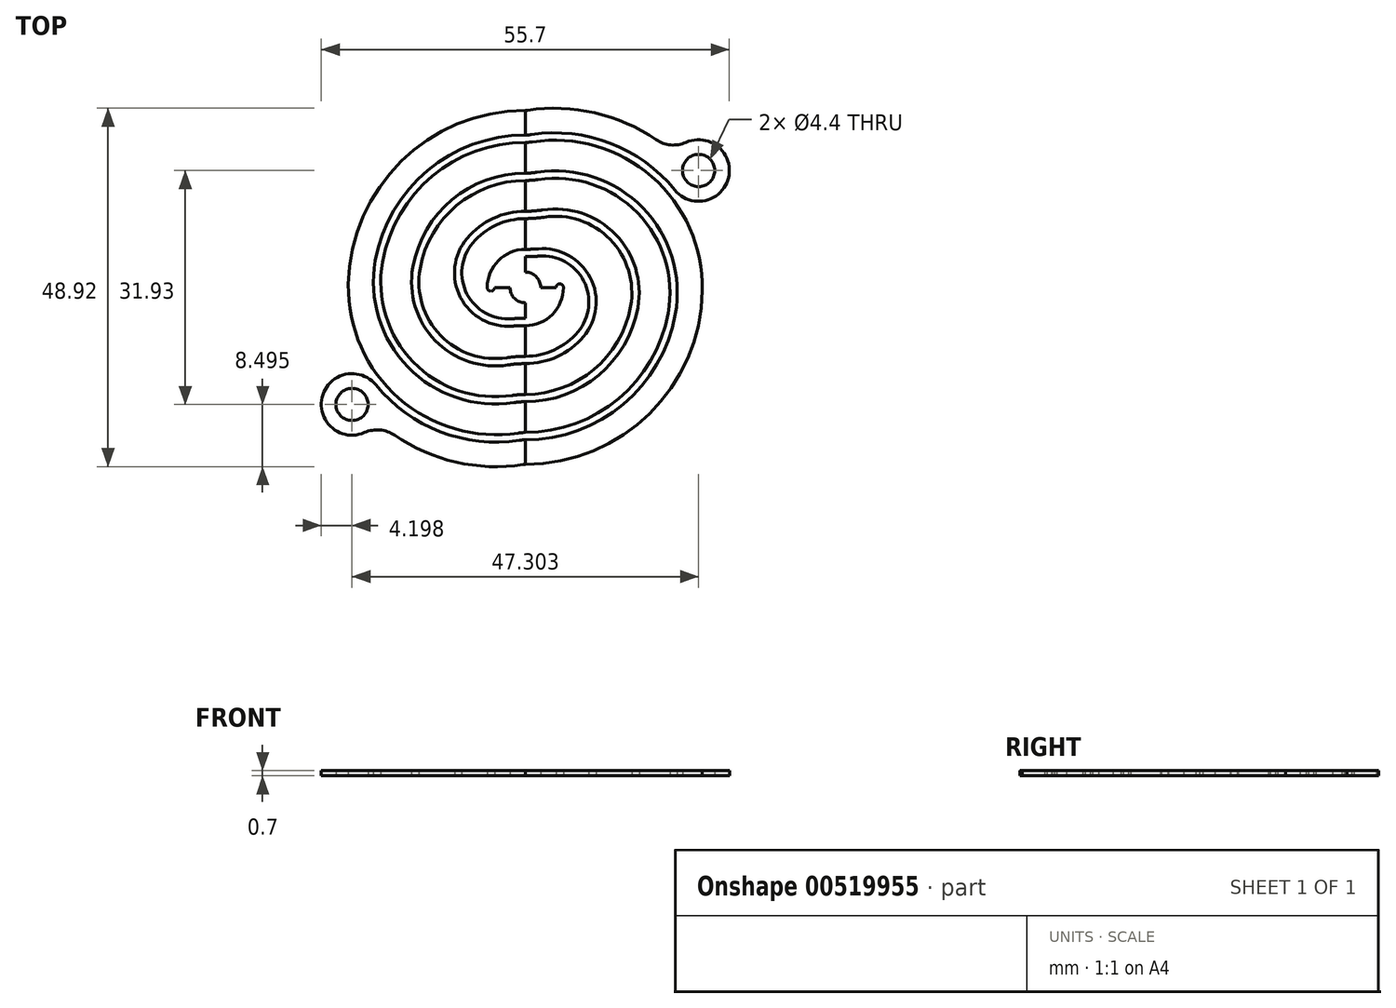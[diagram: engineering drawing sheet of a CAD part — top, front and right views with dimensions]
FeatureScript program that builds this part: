
annotation { "Feature Type Name" : "Feature", "Feature Type Description" : "" }
export const myFeature = defineFeature(function(context is Context, id is Id, definition is map)
    precondition{}
    {
        {
            var Q0;
            Q0=qCreatedBy(makeId("Top.planeOp"),FACE);
            var sketch = newSketch(context, id + "F0", { "sketchPlane" : qUnion([Q0])});
            skCircle(sketch, "E0", {"center": v(0, 0) * mm, "radius": 2.1 * mm, "construction": true});
            skArc(sketch, "E1.0", {"start": v(13.08, 8.5) * mm, "mid": v(13.07, 8.51) * mm, "end": v(13.06, 8.53) * mm, "construction": true});
            skArc(sketch, "E2.0", {"start": v(8.24, 18) * mm, "mid": v(7.74, 18.23) * mm, "end": v(7.23, 18.43) * mm, "construction": true});
            skArc(sketch, "E3.0", {"start": v(0, 20.8) * mm, "mid": v(-14.7, -14.7) * mm, "end": v(20.8, 0) * mm, "construction": true});
            skArc(sketch, "E4.0", {"start": v(-4.81, 23.68) * mm, "mid": v(-12.28, -20.8) * mm, "end": v(23.05, 7.24) * mm, "construction": true});
            skCircle(sketch, "E5.converted", {"center": v(0, 0) * mm, "radius": 4.2 * mm, "construction": true});
            skCircle(sketch, "E6.converted", {"center": v(0, 0) * mm, "radius": 5.2 * mm, "construction": true});
            skArc(sketch, "E7.converted", {"start": v(0, 9.4) * mm, "mid": v(-8.53, -3.96) * mm, "end": v(7.18, -6.07) * mm, "construction": true});
            skArc(sketch, "E8.converted", {"start": v(3.6, 9.75) * mm, "mid": v(3.58, 9.77) * mm, "end": v(3.55, 9.78) * mm, "construction": true});
            skArc(sketch, "E9", {"start": v(0, 14.6) * mm, "mid": v(-4.54, 13.88) * mm, "end": v(-8.63, 11.78) * mm, "construction": true});
            skArc(sketch, "E10", {"start": v(18.7, 16.59) * mm, "mid": v(-23.37, -8.87) * mm, "end": v(25, 0) * mm, "construction": true});
            skCircle(sketch, "E11", {"center": v(0, 26.26) * mm, "radius": 24.16 * mm, "construction": true});
            skCircle(sketch, "E12", {"center": v(0, 26.26) * mm, "radius": 22.06 * mm, "construction": true});
            skCircle(sketch, "E13", {"center": v(0, 26.26) * mm, "radius": 21.06 * mm, "construction": true});
            skArc(sketch, "E14", {"start": v(-3.55, 9.78) * mm, "mid": v(2.73, 9.62) * mm, "end": v(8.63, 11.78) * mm, "construction": true});
            skCircle(sketch, "E15", {"center": v(0, 26.26) * mm, "radius": 11.66 * mm, "construction": true});
            skCircle(sketch, "E16", {"center": v(0, 26.26) * mm, "radius": 10.66 * mm, "construction": true});
            skArc(sketch, "E17", {"start": v(-5.82, 23.45) * mm, "mid": v(-4.67, 21.8) * mm, "end": v(-3.06, 20.57) * mm, "construction": true});
            skLineSegment(sketch, "E18", {"start": v(2.1, 0) * mm, "end": v(4.2, 0) * mm});
            skLineSegment(sketch, "E19", {"start": v(15.6, 0) * mm, "end": v(19.8, 0) * mm});
            skLineSegment(sketch, "E20", {"start": v(-10.4, 0) * mm, "end": v(-14.6, 0) * mm});
            skLineSegment(sketch, "E21", {"start": v(-15.6, 0) * mm, "end": v(-19.8, 0) * mm});
            skLineSegment(sketch, "E22", {"start": v(-20.8, 0) * mm, "end": v(-24.16, 0) * mm});
            skLineSegment(sketch, "E23", {"start": v(4.2, 0) * mm, "end": v(5.2, 0) * mm, "construction": true});
            skArc(sketch, "E24", {"start": v(5.2, 0) * mm, "mid": v(4.7, 0.5) * mm, "end": v(4.2, 0) * mm});
            skArc(sketch, "E25", {"start": v(0, 4.2) * mm, "mid": v(0.92, 4.22) * mm, "end": v(1.84, 4.28) * mm});
            skArc(sketch, "E26", {"start": v(7.18, -6.07) * mm, "mid": v(-8.53, -3.96) * mm, "end": v(0, 9.4) * mm, "construction": true});
            skPoint(sketch, "E27.visualSharp", {"position": v(7.59, 5.55) * mm});
            skArc(sketch, "E27.filletArc", {"start": v(7.18, -6.07) * mm, "mid": v(7.97, 0.89) * mm, "end": v(1.84, 4.28) * mm});
            skArc(sketch, "E28", {"start": v(0, 4.2) * mm, "mid": v(-2.97, 2.97) * mm, "end": v(-4.2, 0) * mm});
            skArc(sketch, "E29", {"start": v(2.1, 0) * mm, "mid": v(0, 2.1) * mm, "end": v(-2.1, 0) * mm});
            skArc(sketch, "E30", {"start": v(0, 5.2) * mm, "mid": v(-3.68, 3.68) * mm, "end": v(-5.2, 0) * mm});
            skArc(sketch, "E31", {"start": v(0, 5.2) * mm, "mid": v(0.88, 5.22) * mm, "end": v(1.76, 5.27) * mm});
            skArc(sketch, "E32", {"start": v(10.26, 1.72) * mm, "mid": v(9.98, 2.92) * mm, "end": v(9.57, 4.08) * mm, "construction": true});
            skPoint(sketch, "E33.visualSharp", {"position": v(7.92, 6.74) * mm});
            skArc(sketch, "E33.filletArc", {"start": v(7.94, -6.71) * mm, "mid": v(8.85, 1.35) * mm, "end": v(1.76, 5.27) * mm});
            skArc(sketch, "E34", {"start": v(0, 9.4) * mm, "mid": v(1.27, 9.45) * mm, "end": v(2.53, 9.6) * mm});
            skArc(sketch, "E35", {"start": v(13.28, 6.07) * mm, "mid": v(13.27, 6.1) * mm, "end": v(13.26, 6.12) * mm, "construction": true});
            skPoint(sketch, "E36.visualSharp", {"position": v(-8.63, 11.78) * mm});
            skArc(sketch, "E37", {"start": v(0, 9.4) * mm, "mid": v(-6.65, 6.65) * mm, "end": v(-9.4, 0) * mm});
            skArc(sketch, "E38.trimOffspring", {"start": v(0, 10.4) * mm, "mid": v(-9.43, -4.38) * mm, "end": v(7.94, -6.71) * mm, "construction": true});
            skArc(sketch, "E39.trimOffspring", {"start": v(0, 10.4) * mm, "mid": v(-9.43, -4.38) * mm, "end": v(7.94, -6.71) * mm});
            skArc(sketch, "E40", {"start": v(-8.63, 11.78) * mm, "mid": v(-6.6, -13.02) * mm, "end": v(14.6, 0) * mm, "construction": true});
            skArc(sketch, "E41", {"start": v(-8.63, 11.78) * mm, "mid": v(-8.18, 12.1) * mm, "end": v(-7.71, 12.4) * mm});
            skArc(sketch, "E42", {"start": v(-8.63, 11.78) * mm, "mid": v(-13.02, 6.6) * mm, "end": v(-14.6, 0) * mm});
            skLineSegment(sketch, "E43", {"start": v(0, 14.6) * mm, "end": v(0, 14.6) * mm});
            skArc(sketch, "E44", {"start": v(17.74, 8.78) * mm, "mid": v(17.57, 9.13) * mm, "end": v(17.38, 9.48) * mm, "construction": true});
            skPoint(sketch, "E45.visualSharp", {"position": v(8.24, 18) * mm});
            skArc(sketch, "E46.trimOffspring", {"start": v(13.08, 8.5) * mm, "mid": v(13.07, 8.51) * mm, "end": v(13.06, 8.53) * mm});
            skArc(sketch, "E47.trimOffspring", {"start": v(0, 15.6) * mm, "mid": v(-11.03, -11.03) * mm, "end": v(15.6, 0) * mm, "construction": true});
            skArc(sketch, "E48", {"start": v(10.26, 1.72) * mm, "mid": v(9.98, 2.92) * mm, "end": v(9.57, 4.08) * mm});
            skArc(sketch, "E49", {"start": v(-9.71, 12.48) * mm, "mid": v(-3.87, 9.85) * mm, "end": v(2.53, 9.6) * mm, "construction": true});
            skArc(sketch, "E50", {"start": v(13.28, 6.07) * mm, "mid": v(13.27, 6.1) * mm, "end": v(13.26, 6.12) * mm});
            skPoint(sketch, "E51.visualSharp", {"position": v(8.63, 11.78) * mm});
            skArc(sketch, "E51.filletArc", {"start": v(14.37, -2.57) * mm, "mid": v(11.57, 6.55) * mm, "end": v(2.53, 9.6) * mm});
            skArc(sketch, "E52.trimOffspring", {"start": v(8.63, 11.78) * mm, "mid": v(10.21, 12.85) * mm, "end": v(11.66, 14.09) * mm, "construction": true});
            skArc(sketch, "E53", {"start": v(0, 14.6) * mm, "mid": v(-4.01, 14.04) * mm, "end": v(-7.71, 12.4) * mm});
            skArc(sketch, "E54", {"start": v(0, 15.6) * mm, "mid": v(-11.03, 11.03) * mm, "end": v(-15.6, 0) * mm});
            skArc(sketch, "E55", {"start": v(0, 14.6) * mm, "mid": v(0.88, 14.63) * mm, "end": v(1.75, 14.73) * mm});
            skCircle(sketch, "E56", {"center": v(0, 26.26) * mm, "radius": 15.86 * mm, "construction": true});
            skArc(sketch, "E57", {"start": v(0, 10.4) * mm, "mid": v(1.2, 10.44) * mm, "end": v(2.38, 10.58) * mm});
            skPoint(sketch, "E58.visualSharp", {"position": v(8.66, 12.97) * mm});
            skArc(sketch, "E58.filletArc", {"start": v(15.36, -2.75) * mm, "mid": v(12.3, 7.25) * mm, "end": v(2.38, 10.58) * mm});
            skArc(sketch, "E59", {"start": v(17.74, 8.78) * mm, "mid": v(17.57, 9.13) * mm, "end": v(17.38, 9.48) * mm});
            skArc(sketch, "E60.filletArc", {"start": v(19.5, -3.49) * mm, "mid": v(15.3, 10.18) * mm, "end": v(1.75, 14.73) * mm});
            skArc(sketch, "E61", {"start": v(0, 15.6) * mm, "mid": v(0.8, 15.63) * mm, "end": v(1.6, 15.72) * mm});
            skArc(sketch, "E62", {"start": v(17.42, 11.37) * mm, "mid": v(17.17, 11.74) * mm, "end": v(16.92, 12.1) * mm});
            skPoint(sketch, "E63.visualSharp", {"position": v(8, 19.2) * mm});
            skArc(sketch, "E63.filletArc", {"start": v(20.47, -3.67) * mm, "mid": v(16.02, 10.88) * mm, "end": v(1.6, 15.72) * mm});
            skArc(sketch, "E64", {"start": v(0, 19.8) * mm, "mid": v(-14, 14) * mm, "end": v(-19.8, 0) * mm});
            skArc(sketch, "E65", {"start": v(0, 19.8) * mm, "mid": v(1.58, 32.52) * mm, "end": v(-3.06, 20.57) * mm, "construction": true});
            skArc(sketch, "E66.trimOffspring", {"start": v(12.7, 15.18) * mm, "mid": v(12.32, 15.5) * mm, "end": v(11.93, 15.8) * mm, "construction": true});
            skArc(sketch, "E67.trimOffspring", {"start": v(16.58, 10.82) * mm, "mid": v(16.41, 11.08) * mm, "end": v(16.24, 11.33) * mm, "construction": true});
            skArc(sketch, "E68", {"start": v(24.16, 0) * mm, "mid": v(23.88, 3.66) * mm, "end": v(23.05, 7.24) * mm});
            skPoint(sketch, "E69.visualSharp", {"position": v(5.82, 23.45) * mm});
            skArc(sketch, "E70.trimOffspring", {"start": v(11.66, 14.09) * mm, "mid": v(-1.26, 43.07) * mm, "end": v(-9.71, 12.48) * mm, "construction": true});
            skArc(sketch, "E71.trimOffspring", {"start": v(10.86, 13.37) * mm, "mid": v(11.27, 13.72) * mm, "end": v(11.66, 14.09) * mm, "construction": true});
            skArc(sketch, "E72", {"start": v(0, 20.8) * mm, "mid": v(-14.7, 14.7) * mm, "end": v(-20.8, 0) * mm});
            skArc(sketch, "E73", {"start": v(0, 24.16) * mm, "mid": v(-17.08, 17.08) * mm, "end": v(-24.16, 0) * mm});
            skArc(sketch, "E74", {"start": v(0, 20.8) * mm, "mid": v(0.41, 20.82) * mm, "end": v(0.82, 20.86) * mm});
            skArc(sketch, "E75", {"start": v(4.81, 23.68) * mm, "mid": v(5, 24.06) * mm, "end": v(5.16, 24.46) * mm});
            skCircle(sketch, "E76.converted", {"center": v(0, 26.26) * mm, "radius": 5.46 * mm, "construction": true});
            skArc(sketch, "E77", {"start": v(0, 19.8) * mm, "mid": v(0.49, 19.82) * mm, "end": v(0.97, 19.87) * mm});
            skArc(sketch, "E78.filletArc", {"start": v(24.16, -0.4) * mm, "mid": v(17.27, 15.12) * mm, "end": v(0.97, 19.87) * mm});
            skArc(sketch, "E79.0", {"start": v(20.4, 13.31) * mm, "mid": v(11.6, 19.68) * mm, "end": v(0.82, 20.86) * mm});
            skCircle(sketch, "E80.converted", {"center": v(0, 26.26) * mm, "radius": 2.1 * mm, "construction": true});
            skArc(sketch, "E81.0", {"start": v(22.1, 16.48) * mm, "mid": v(21.88, 16.72) * mm, "end": v(21.66, 16.95) * mm, "construction": true});
            skArc(sketch, "E82", {"start": v(0, 24.16) * mm, "mid": v(0.16, 24.17) * mm, "end": v(0.31, 24.18) * mm});
            skLineSegment(sketch, "E83", {"start": v(0, 0) * mm, "end": v(12.23, 7.98) * mm, "construction": true});
            skArc(sketch, "E84.trimOffspring", {"start": v(17.85, 20.17) * mm, "mid": v(9.46, 23.84) * mm, "end": v(0.31, 24.18) * mm});
            skArc(sketch, "E85", {"start": v(20.4, 13.31) * mm, "mid": v(27.74, 15) * mm, "end": v(21.94, 19.8) * mm});
            skCircle(sketch, "E86", {"center": v(23.65, 15.97) * mm, "radius": 2.2 * mm});
            skPoint(sketch, "E87.visualSharp", {"position": v(20.2, 18.35) * mm});
            skArc(sketch, "E87.filletArc", {"start": v(17.85, 20.17) * mm, "mid": v(19.85, 19.45) * mm, "end": v(21.94, 19.8) * mm});
            skLineSegment(sketch, "E88", {"start": v(0, -5.2) * mm, "end": v(0, -9.4) * mm});
            skLineSegment(sketch, "E89", {"start": v(0, -10.4) * mm, "end": v(0, -14.6) * mm});
            skLineSegment(sketch, "E90", {"start": v(0, -15.6) * mm, "end": v(0, -19.8) * mm});
            skLineSegment(sketch, "E91", {"start": v(0, -20.8) * mm, "end": v(0, -24.16) * mm});
            skArc(sketch, "E92", {"start": v(0, -5.2) * mm, "mid": v(3.68, -3.68) * mm, "end": v(5.2, 0) * mm});
            skArc(sketch, "E93", {"start": v(-1.53, -9.28) * mm, "mid": v(3.25, -8.82) * mm, "end": v(7.18, -6.07) * mm});
            skLineSegment(sketch, "E94", {"start": v(0, 2.1) * mm, "end": v(0, 4.2) * mm});
            skLineSegment(sketch, "E95", {"start": v(0, 10.4) * mm, "end": v(0, 14.6) * mm});
            skLineSegment(sketch, "E96", {"start": v(0, 15.6) * mm, "end": v(0, 19.8) * mm});
            skLineSegment(sketch, "E97", {"start": v(0, 20.8) * mm, "end": v(0, 24.16) * mm});
            skLineSegment(sketch, "E98", {"start": v(0, 5.2) * mm, "end": v(0, 9.4) * mm});
            skArc(sketch, "E99", {"start": v(0, -14.6) * mm, "mid": v(10.32, -10.32) * mm, "end": v(14.6, 0) * mm});
            skArc(sketch, "E100.trimOffspring", {"start": v(0, 9.4) * mm, "mid": v(-8.53, -3.96) * mm, "end": v(7.18, -6.07) * mm});
            skArc(sketch, "E101.trimOffspring", {"start": v(3.6, 9.75) * mm, "mid": v(3.58, 9.77) * mm, "end": v(3.55, 9.78) * mm});
            skArc(sketch, "E102.trimOffspring", {"start": v(8.7, 5.68) * mm, "mid": v(8.63, 5.8) * mm, "end": v(8.55, 5.92) * mm});
            skArc(sketch, "E103.trimOffspring", {"start": v(7.87, 5.14) * mm, "mid": v(7.73, 5.34) * mm, "end": v(7.59, 5.55) * mm});
            skArc(sketch, "E104.trimOffspring", {"start": v(9.4, -0.04) * mm, "mid": v(9.36, 0.85) * mm, "end": v(9.24, 1.72) * mm, "construction": true});
            skArc(sketch, "E105.trimOffspring", {"start": v(9.4, -0.04) * mm, "mid": v(9.36, 0.85) * mm, "end": v(9.24, 1.72) * mm});
            skArc(sketch, "E106.trimOffspring", {"start": v(12.26, 7.92) * mm, "mid": v(12.25, 7.95) * mm, "end": v(12.23, 7.98) * mm, "construction": true});
            skArc(sketch, "E107.trimOffspring", {"start": v(12.26, 7.92) * mm, "mid": v(12.25, 7.95) * mm, "end": v(12.23, 7.98) * mm});
            skLineSegment(sketch, "E108.trimOffspring", {"start": v(13.06, 8.53) * mm, "end": v(23.22, 15.16) * mm, "construction": true});
            skArc(sketch, "E109.trimOffspring", {"start": v(0, 14.6) * mm, "mid": v(-11.2, -9.37) * mm, "end": v(14.37, -2.57) * mm});
            skArc(sketch, "E110.trimOffspring", {"start": v(0, 15.6) * mm, "mid": v(-11.96, -10.01) * mm, "end": v(15.36, -2.75) * mm});
            skArc(sketch, "E111.trimOffspring", {"start": v(0, 19.8) * mm, "mid": v(4.57, 21.7) * mm, "end": v(6.46, 26.26) * mm, "construction": true});
            skArc(sketch, "E112.trimOffspring", {"start": v(0, 20.8) * mm, "mid": v(-15.95, -13.35) * mm, "end": v(20.47, -3.67) * mm});
            skArc(sketch, "E113.trimOffspring", {"start": v(0, 19.8) * mm, "mid": v(-16.25, -11.32) * mm, "end": v(18.57, -6.86) * mm, "construction": true});
            skArc(sketch, "E114.trimOffspring", {"start": v(0, 19.8) * mm, "mid": v(-14, -14) * mm, "end": v(19.8, 0) * mm, "construction": true});
            skArc(sketch, "E115.trimOffspring", {"start": v(0, 19.8) * mm, "mid": v(-15.18, -12.7) * mm, "end": v(19.5, -3.49) * mm, "construction": true});
            skArc(sketch, "E116.trimOffspring", {"start": v(0, 19.8) * mm, "mid": v(-15.18, -12.7) * mm, "end": v(19.5, -3.49) * mm});
            skArc(sketch, "E117.trimOffspring", {"start": v(5.58, 20.04) * mm, "mid": v(4.33, 20.34) * mm, "end": v(3.06, 20.57) * mm, "construction": true});
            skArc(sketch, "E118.trimOffspring", {"start": v(5.58, 20.04) * mm, "mid": v(4.33, 20.34) * mm, "end": v(3.06, 20.57) * mm});
            skArc(sketch, "E119", {"start": v(0, -24.16) * mm, "mid": v(19.48, -14.3) * mm, "end": v(23.05, 7.24) * mm});
            skArc(sketch, "E120.trimOffspring", {"start": v(8.24, 18) * mm, "mid": v(7.74, 18.23) * mm, "end": v(7.23, 18.43) * mm});
            skArc(sketch, "E121.trimOffspring", {"start": v(8.94, 18.78) * mm, "mid": v(8.47, 19) * mm, "end": v(8, 19.2) * mm, "construction": true});
            skArc(sketch, "E122.trimOffspring", {"start": v(13.34, 15.96) * mm, "mid": v(12.96, 16.27) * mm, "end": v(12.56, 16.58) * mm, "construction": true});
            skArc(sketch, "E123.trimOffspring", {"start": v(13.34, 15.96) * mm, "mid": v(12.96, 16.27) * mm, "end": v(12.56, 16.58) * mm});
            skArc(sketch, "E124.trimOffspring", {"start": v(17.42, 11.37) * mm, "mid": v(17.17, 11.74) * mm, "end": v(16.92, 12.1) * mm, "construction": true});
            skArc(sketch, "E125.trimOffspring", {"start": v(12.7, 15.18) * mm, "mid": v(12.32, 15.5) * mm, "end": v(11.93, 15.8) * mm});
            skArc(sketch, "E126.trimOffspring", {"start": v(16.58, 10.82) * mm, "mid": v(16.41, 11.08) * mm, "end": v(16.24, 11.33) * mm});
            skArc(sketch, "E127.trimOffspring", {"start": v(20.28, 13.13) * mm, "mid": v(19.33, 14.5) * mm, "end": v(18.28, 15.8) * mm, "construction": true});
            skArc(sketch, "E128.trimOffspring", {"start": v(20.28, 13.13) * mm, "mid": v(19.33, 14.5) * mm, "end": v(18.28, 15.8) * mm});
            skArc(sketch, "E129.trimOffspring", {"start": v(10.71, 21.66) * mm, "mid": v(10.26, 21.87) * mm, "end": v(9.8, 22.08) * mm, "construction": true});
            skArc(sketch, "E130.trimOffspring", {"start": v(10.71, 21.66) * mm, "mid": v(10.26, 21.87) * mm, "end": v(9.8, 22.08) * mm});
            skArc(sketch, "E131.trimOffspring", {"start": v(5.82, 23.45) * mm, "mid": v(5.31, 23.57) * mm, "end": v(4.81, 23.68) * mm});
            skArc(sketch, "E132.trimOffspring", {"start": v(15.14, 18.83) * mm, "mid": v(14.73, 19.15) * mm, "end": v(14.33, 19.45) * mm, "construction": true});
            skArc(sketch, "E133.trimOffspring", {"start": v(15.14, 18.83) * mm, "mid": v(14.73, 19.15) * mm, "end": v(14.33, 19.45) * mm});
            skArc(sketch, "E134.trimOffspring", {"start": v(0, 24.16) * mm, "mid": v(-17.22, -16.94) * mm, "end": v(24.16, -0.4) * mm});
            skSolve(sketch);
        }
        {
            var Q0;
            Q0=makeQuery(id+"F0.imprint","IMPRINT",FACE,{"disambiguationData":[TD([[makeQuery(id+"F0.imprint","IMPRINT",EDGE,{"derivedFrom":sQuery(id+"F0.wireOp",EDGE,"C1ZH9qWL-1q6U-ss44-XQ4E-Uqg7t3fqfPqc")}),-1.0]])]});
            var Q1;
            Q1=makeQuery(id+"F0.imprint","IMPRINT",FACE,{"disambiguationData":[TD([[makeQuery(id+"F0.imprint","IMPRINT",EDGE,{"derivedFrom":sQuery(id+"F0.wireOp",EDGE,"E18")}),1.0]])]});
            var Q2;
            {var subQ1=sQuery(id+"F0.wireOp",EDGE,"E19");Q2=makeQuery(id+"F0.imprint","IMPRINT",FACE,{"disambiguationData":[TD([[makeQuery(id+"F0.imprint","IMPRINT",EDGE,{"derivedFrom":subQ1}),1.0]])]});}
            var Q3;
            Q3=makeQuery(id+"F0.imprint","IMPRINT",FACE,{"disambiguationData":[TD([[makeQuery(id+"F0.imprint","IMPRINT",EDGE,{"derivedFrom":sQuery(id+"F0.wireOp",EDGE,"WrsLuIRp-1QCu-0zp7-bs5D-gCrvSLc5zUkS")}),1.0]])]});
            var Q4;
            {var subQ4=sQuery(id+"F0.wireOp",EDGE,"E31");Q4=makeQuery(id+"F0.imprint","IMPRINT",FACE,{"disambiguationData":[TD([[makeQuery(id+"F0.imprint","IMPRINT",EDGE,{"derivedFrom":subQ4}),1.0]])]});}
            var Q5;
            {var subQ5=sQuery(id+"F0.wireOp",EDGE,"E55");Q5=makeQuery(id+"F0.imprint","IMPRINT",FACE,{"disambiguationData":[TD([[makeQuery(id+"F0.imprint","IMPRINT",EDGE,{"derivedFrom":subQ5}),-1.0]])]});}
            var Q6;
            {var subQ3=sQuery(id+"F0.wireOp",EDGE,"E61");Q6=makeQuery(id+"F0.imprint","IMPRINT",FACE,{"disambiguationData":[TD([[makeQuery(id+"F0.imprint","IMPRINT",EDGE,{"derivedFrom":subQ3}),1.0]])]});}
            var Q7;
            {var subQ4=sQuery(id+"F0.wireOp",EDGE,"E74");Q7=makeQuery(id+"F0.imprint","IMPRINT",FACE,{"disambiguationData":[TD([[makeQuery(id+"F0.imprint","IMPRINT",EDGE,{"derivedFrom":subQ4}),1.0]])]});}
            extrude(context, id + "F1", {"entities" : qUnion([Q0, Q1, Q2, Q3, Q4, Q5, Q6, Q7]), "depth" : .7 * mm, "offsetDistance" : 25 * mm});
        }
        {
            var Q0;
            Q0=makeQuery(id+"F1.opExtrude","SWEPT_BODY",BODY,{"disambiguationData":[OSD([sQuery(id+"F0.wireOp",EDGE,"E18"),sQuery(id+"F0.wireOp",EDGE,"n5tJrcJz-reaJ-LP6T-iDj3-x99ptH7I2xX8"),sQuery(id+"F0.wireOp",EDGE,"R9k50rTa-Cjw7-9YF7-ql30-938Zlf7ctmgj"),sQuery(id+"F0.wireOp",EDGE,"E24"),sQuery(id+"F0.wireOp",EDGE,"E25"),sQuery(id+"F0.wireOp",EDGE,"E27.filletArc"),sQuery(id+"F0.wireOp",EDGE,"E28"),sQuery(id+"F0.wireOp",EDGE,"E29")])]});
            var Q1;
            Q1=makeQuery(id+"F1.opExtrude","SWEPT_BODY",BODY,{"disambiguationData":[OSD([sQuery(id+"F0.wireOp",EDGE,"ThBs2scR-JBao-TLdy-ChiO-wfkyVLInF4wm"),sQuery(id+"F0.wireOp",EDGE,"C1ZH9qWL-1q6U-ss44-XQ4E-Uqg7t3fqfPqc"),sQuery(id+"F0.wireOp",EDGE,"E30"),sQuery(id+"F0.wireOp",EDGE,"E31"),sQuery(id+"F0.wireOp",EDGE,"E33.filletArc"),sQuery(id+"F0.wireOp",EDGE,"E34"),sQuery(id+"F0.wireOp",EDGE,"E37"),sQuery(id+"F0.wireOp",EDGE,"E48"),sQuery(id+"F0.wireOp",EDGE,"E50"),sQuery(id+"F0.wireOp",EDGE,"E51.filletArc")])]});
            var Q2;
            Q2=makeQuery(id+"F1.opExtrude","SWEPT_BODY",BODY,{"disambiguationData":[OSD([sQuery(id+"F0.wireOp",EDGE,"E19"),sQuery(id+"F0.wireOp",EDGE,"E20"),sQuery(id+"F0.wireOp",EDGE,"E39.trimOffspring"),sQuery(id+"F0.wireOp",EDGE,"E41"),sQuery(id+"F0.wireOp",EDGE,"E42"),sQuery(id+"F0.wireOp",EDGE,"E53"),sQuery(id+"F0.wireOp",EDGE,"E55"),sQuery(id+"F0.wireOp",EDGE,"E46.trimOffspring"),sQuery(id+"F0.wireOp",EDGE,"E57"),sQuery(id+"F0.wireOp",EDGE,"E58.filletArc"),sQuery(id+"F0.wireOp",EDGE,"E59"),sQuery(id+"F0.wireOp",EDGE,"E60.filletArc")])]});
            var Q3;
            Q3=makeQuery(id+"F1.opExtrude","SWEPT_BODY",BODY,{"disambiguationData":[OSD([sQuery(id+"F0.wireOp",EDGE,"WrsLuIRp-1QCu-0zp7-bs5D-gCrvSLc5zUkS"),sQuery(id+"F0.wireOp",EDGE,"E21"),sQuery(id+"F0.wireOp",EDGE,"E54"),sQuery(id+"F0.wireOp",EDGE,"E61"),sQuery(id+"F0.wireOp",EDGE,"E62"),sQuery(id+"F0.wireOp",EDGE,"E63.filletArc"),sQuery(id+"F0.wireOp",EDGE,"E64"),sQuery(id+"F0.wireOp",EDGE,"E68"),sQuery(id+"F0.wireOp",EDGE,"E77"),sQuery(id+"F0.wireOp",EDGE,"E78.filletArc")])]});
            var Q4;
            Q4=makeQuery(id+"F1.opExtrude","SWEPT_BODY",BODY,{"disambiguationData":[OSD([sQuery(id+"F0.wireOp",EDGE,"E22"),sQuery(id+"F0.wireOp",EDGE,"E72"),sQuery(id+"F0.wireOp",EDGE,"E73"),sQuery(id+"F0.wireOp",EDGE,"E74"),sQuery(id+"F0.wireOp",EDGE,"E79.0"),sQuery(id+"F0.wireOp",EDGE,"E82"),sQuery(id+"F0.wireOp",EDGE,"9NUbP7Mr-0lKH-UUtn-VFz5-Uik6tJHT7edk"),sQuery(id+"F0.wireOp",EDGE,"E84.trimOffspring"),sQuery(id+"F0.wireOp",EDGE,"eKzqWYXa-ZtuT-rVpZ-CJWK-zkNVA6rLTH0m")])]});
            var Q5;
            Q5=sQuery(id+"F0.wireOp",EDGE,"E0");
            circularPattern(context, id + "F2", {"entities" : qUnion([Q0, Q1, Q2, Q3, Q4]), "axis" : qUnion([Q5]), "angle" : 180 * degree, "instanceCount" : 2, "equalSpace" : true});
        }
    });
